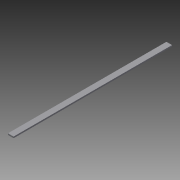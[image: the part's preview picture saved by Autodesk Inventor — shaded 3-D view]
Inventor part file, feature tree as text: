
AUTODESK INVENTOR PART (.ipt)
format: ipt  version: 2015 (Build 190159000, 159)  size: 75,264 bytes
history: native  units: in
note: dims shown in document units (in); Inventor stores cm internally (conversion verified against a paired STEP export)
features: extrude x2, sketch x2
ambient origin geometry x8: Origin, YZ Plane, XZ Plane, XY Plane, X Axis, Y Axis, Z Axis, Center Point
bodies: Solid1 (feature_tree)
feature tree (4):
  extrude  "Extrusion1"  Depth=0.125in
  extrude  "Extrusion2"  Depth=14.0in TaperAngle=0.0deg
  sketch  "Sketch1"  dims[d0=1.5in d1=0.125in]
  sketch  "Sketch2"  dims[d2=14.0in d3=0.0in d4=1.0in d5=0.0in]
